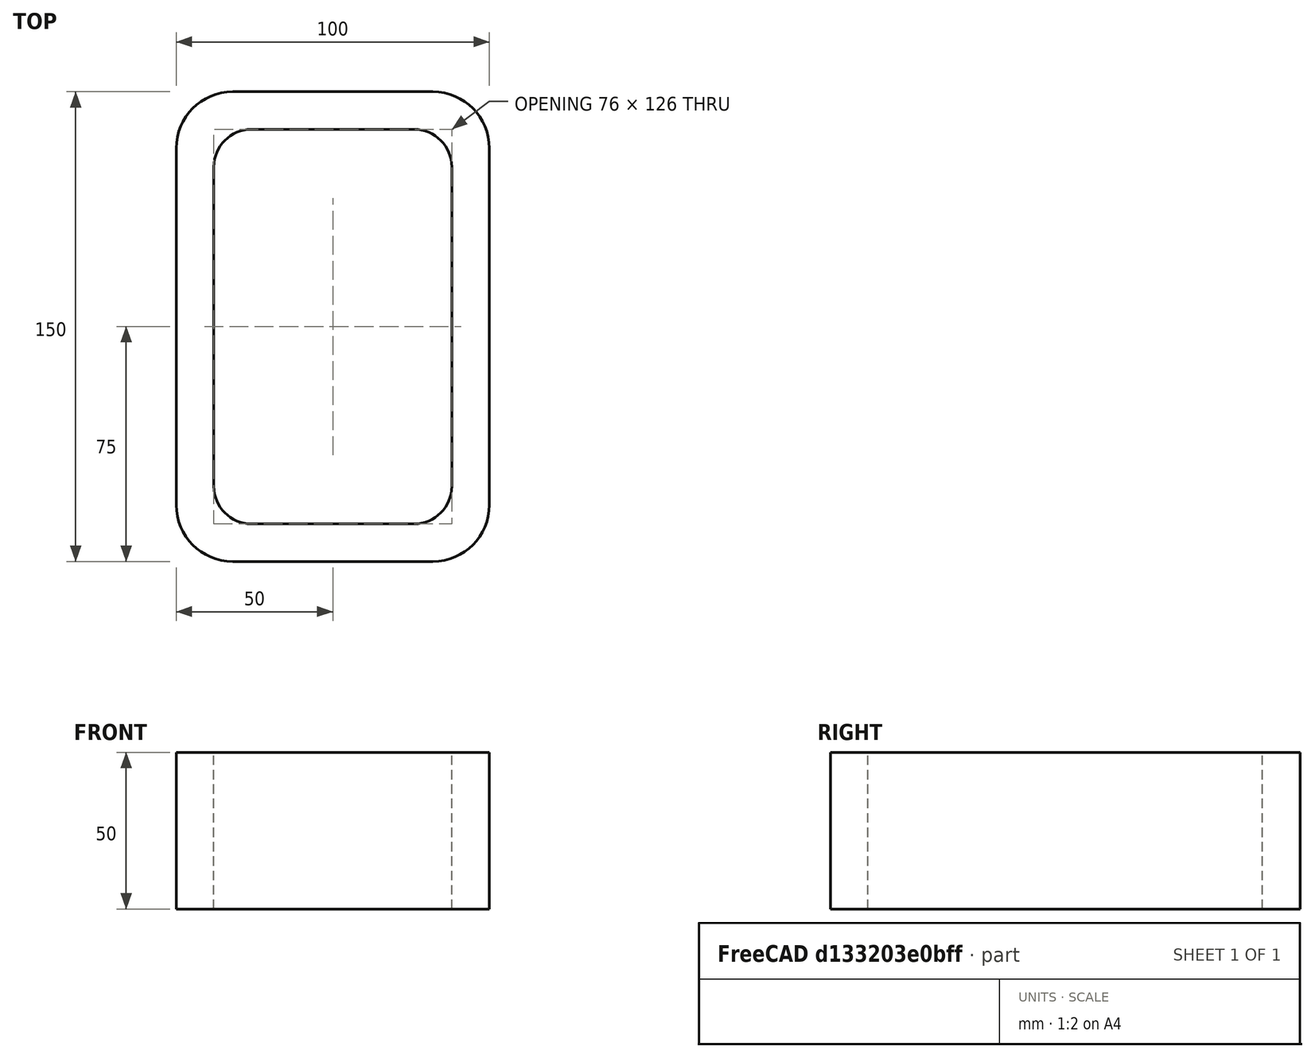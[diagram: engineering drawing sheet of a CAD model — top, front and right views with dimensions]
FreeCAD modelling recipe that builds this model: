
FCSTD DOCUMENT  (FreeCAD 0.15R4671 (Git))
Label: Rectangular hollow section 150x100x12 EN10219 S235JRH
License: All rights reserved
LicenseURL: http://en.wikipedia.org/wiki/All_rights_reserved
objects: Sketcher::SketchObject×1, Part::Extrusion×1
note: 2 computed .brp shape members not serialized (recipe doc carries the construction recipe); baked Part::Feature solids carry a one-line shape summary decoded from their .brp

FEATURE [Sketcher::SketchObject] Sketch
  sketch-geometry (16):
    g0: LineSegment StartX=-26 StartY=63 StartZ=0 EndX=26 EndY=63 EndZ=0
    g1: LineSegment StartX=38 StartY=51 StartZ=0 EndX=38 EndY=-51 EndZ=0
    g2: LineSegment StartX=26 StartY=-63 StartZ=0 EndX=-26 EndY=-63 EndZ=0
    g3: LineSegment StartX=-38 StartY=-51 StartZ=0 EndX=-38 EndY=51 EndZ=0
    g4: LineSegment StartX=-32 StartY=75 StartZ=0 EndX=32 EndY=75 EndZ=0
    g5: LineSegment StartX=50 StartY=57 StartZ=0 EndX=50 EndY=-57 EndZ=0
    g6: LineSegment StartX=32 StartY=-75 StartZ=0 EndX=-32 EndY=-75 EndZ=0
    g7: LineSegment StartX=-50 StartY=-57 StartZ=0 EndX=-50 EndY=57 EndZ=0
    g8: ArcOfCircle CenterX=-26 CenterY=51 CenterZ=0 NormalX=0 NormalY=0 NormalZ=1 Radius=12 StartAngle=1.5708 EndAngle=3.14159
    g9: ArcOfCircle CenterX=26 CenterY=51 CenterZ=0 NormalX=0 NormalY=0 NormalZ=1 Radius=12 StartAngle=0 EndAngle=1.5708
    g10: ArcOfCircle CenterX=26 CenterY=-51 CenterZ=0 NormalX=0 NormalY=0 NormalZ=1 Radius=12 StartAngle=4.71239 EndAngle=6.28319
    g11: ArcOfCircle CenterX=-26 CenterY=-51 CenterZ=0 NormalX=0 NormalY=0 NormalZ=1 Radius=12 StartAngle=3.14159 EndAngle=4.71239
    g12: ArcOfCircle CenterX=32 CenterY=57 CenterZ=0 NormalX=0 NormalY=0 NormalZ=1 Radius=18 StartAngle=0 EndAngle=1.5708
    g13: ArcOfCircle CenterX=32 CenterY=-57 CenterZ=0 NormalX=0 NormalY=0 NormalZ=1 Radius=18 StartAngle=4.71239 EndAngle=6.28319
    g14: ArcOfCircle CenterX=-32 CenterY=-57 CenterZ=0 NormalX=0 NormalY=0 NormalZ=1 Radius=18 StartAngle=3.14159 EndAngle=4.71239
    g15: ArcOfCircle CenterX=-32 CenterY=57 CenterZ=0 NormalX=0 NormalY=0 NormalZ=1 Radius=18 StartAngle=1.5708 EndAngle=3.14159
  constraints (36):
    c: Horizontal(g2)
    c: Vertical(g3)
    c: Horizontal(g6)
    c: Vertical(g7)
    c: Tangent(g3,g8) = 1.5708
    c: Tangent(g0,g8) = 1.5708
    c: Tangent(g0,g9) = 1.5708
    c: Tangent(g1,g9) = 1.5708
    c: Tangent(g1,g10) = 1.5708
    c: Tangent(g2,g10) = 1.5708
    c: Tangent(g2,g11) = 1.5708
    c: Tangent(g3,g11) = 1.5708
    c: Tangent(g4,g12) = 1.5708
    c: Tangent(g5,g12) = 1.5708
    c: Tangent(g5,g13) = 1.5708
    c: Tangent(g6,g13) = 1.5708
    c: Tangent(g6,g14) = 1.5708
    c: Tangent(g7,g14) = 1.5708
    c: Tangent(g7,g15) = 1.5708
    c: Tangent(g4,g15) = 1.5708
    c: Equal(g9,g8)
    c: Equal(g9,g11)
    c: Equal(g9,g10)
    c: Equal(g12,g15)
    c: Equal(g12,g14)
    c: Equal(g12,g13)
    c: Symmetric(g4,g6,g-1)
    c: Symmetric(g7,g5,g-2)
    c: DistanceY(g4,g6) = -150
    c: DistanceX(g7,g5) = 100
    c: Symmetric(g3,g1,g-2)
    c: Symmetric(g0,g2,g-1)
    c: DistanceY(g0,g4) = 12
    c: DistanceX(g5,g1) = -12
    c: Radius(g9) = 12
    c: Radius(g12) = 18
FEATURE [Part::Extrusion] Extrude  label="Rectangular hollow section 150x100x12 EN10219 S235JRH"
  Base = -> Sketch
  Dir = (0,0,50)
  Solid = true
